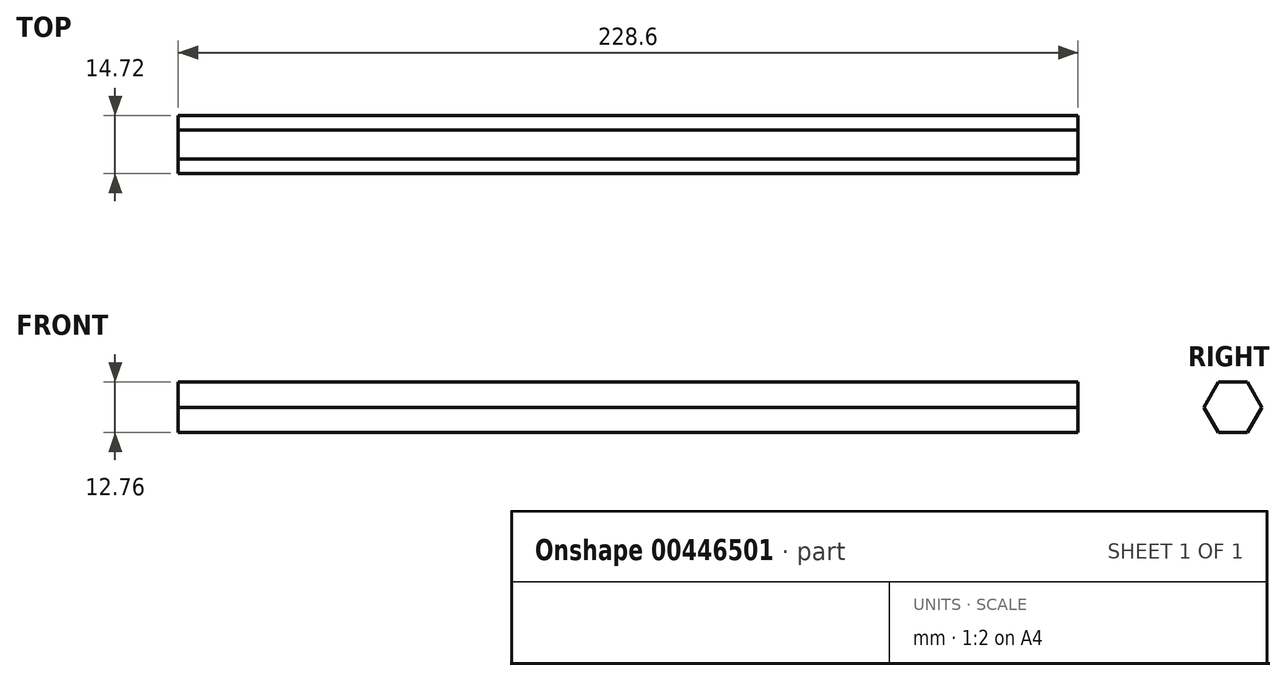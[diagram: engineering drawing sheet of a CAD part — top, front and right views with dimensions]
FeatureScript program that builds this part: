
annotation { "Feature Type Name" : "Feature", "Feature Type Description" : "" }
export const myFeature = defineFeature(function(context is Context, id is Id, definition is map)
    precondition{}
    {
        {
            var Q0;
            Q0=qCreatedBy(makeId("Right.planeOp"),FACE);
            var sketch = newSketch(context, id + "F0", { "sketchPlane" : qUnion([Q0])});
            skCircle(sketch, "E0.cCircle", {"center": v(0, 0) * mm, "radius": 6.38 * mm, "construction": true});
            skLineSegment(sketch, "E0.0", {"start": v(3.68, 6.38) * mm, "end": v(7.36, 0) * mm});
            skLineSegment(sketch, "E0.1", {"start": v(7.36, 0) * mm, "end": v(3.68, -6.38) * mm});
            skLineSegment(sketch, "E0.2", {"start": v(3.68, -6.38) * mm, "end": v(-3.68, -6.38) * mm});
            skLineSegment(sketch, "E0.3", {"start": v(-3.68, -6.38) * mm, "end": v(-7.36, 0) * mm});
            skLineSegment(sketch, "E0.4", {"start": v(-7.36, 0) * mm, "end": v(-3.68, 6.38) * mm});
            skLineSegment(sketch, "E0.5", {"start": v(-3.68, 6.38) * mm, "end": v(3.68, 6.38) * mm});
            skPoint(sketch, "E0.0.midPoint", {"position": v(5.52, 3.19) * mm});
            skSolve(sketch);
        }
        {
            var Q0;
            Q0=makeQuery(id+"F0.imprint","IMPRINT",FACE,{"disambiguationData":[TD([[makeQuery(id+"F0.imprint","IMPRINT",EDGE,{"derivedFrom":sQuery(id+"F0.wireOp",EDGE,"E0.0")}),-1.0]])]});
            extrude(context, id + "F1", {"entities" : qUnion([Q0]), "depth" : 228.6 * mm, "symmetric" : true});
        }
    });
